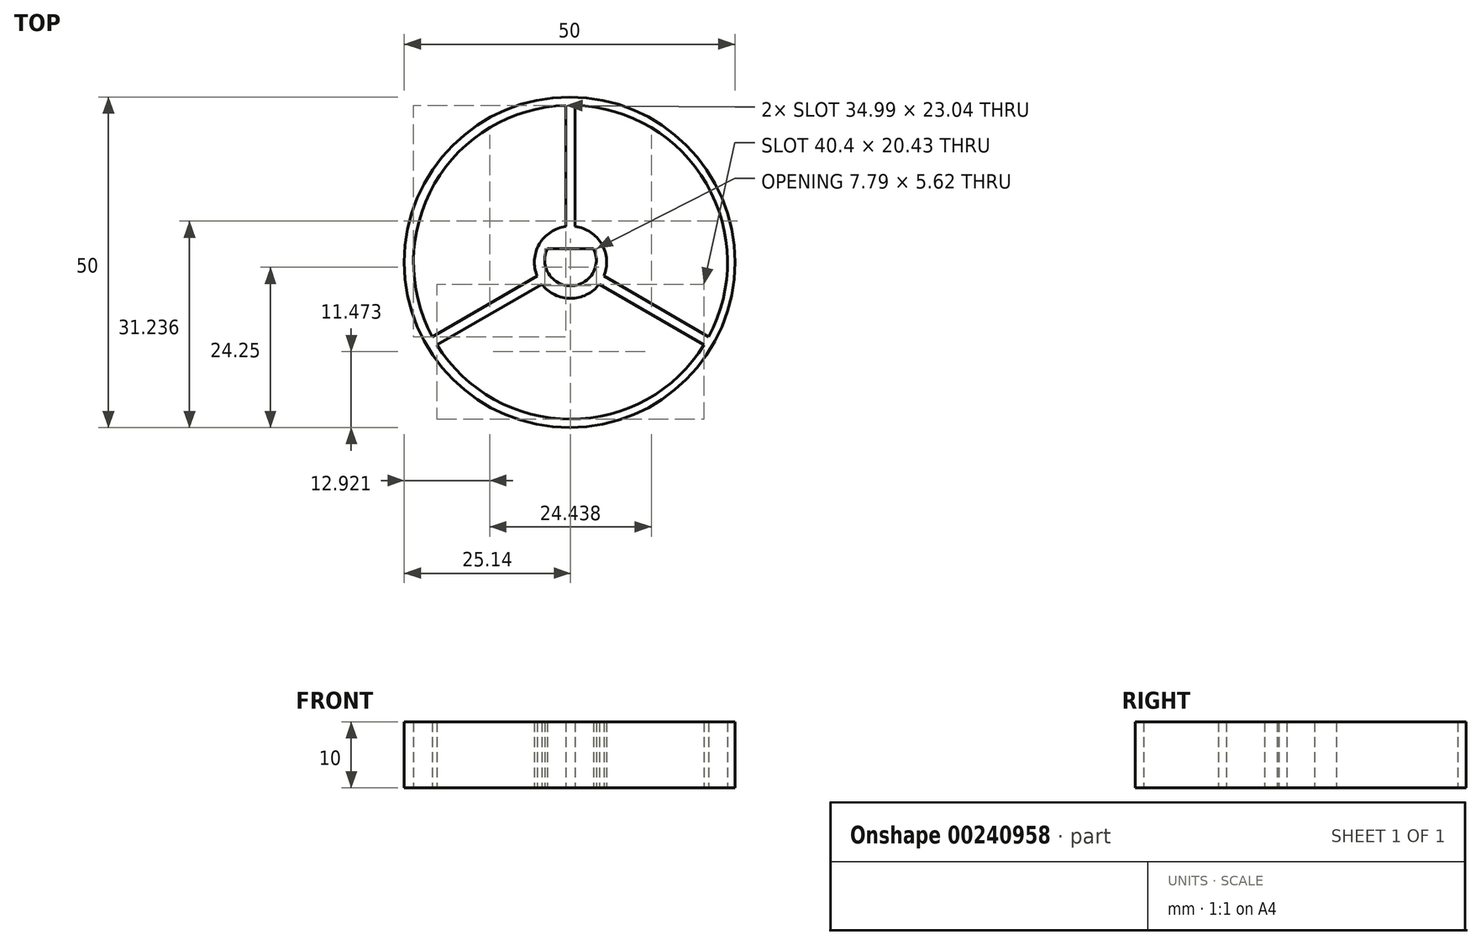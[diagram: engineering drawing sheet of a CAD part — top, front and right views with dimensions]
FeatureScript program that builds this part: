
annotation { "Feature Type Name" : "Feature", "Feature Type Description" : "" }
export const myFeature = defineFeature(function(context is Context, id is Id, definition is map)
    precondition{}
    {
        {
            var Q0;
            Q0=qCreatedBy(makeId("Top.planeOp"),FACE);
            var sketch = newSketch(context, id + "F0", { "sketchPlane" : qUnion([Q0])});
            skCircle(sketch, "E0", {"center": v(0, 0) * mm, "radius": 23.74 * mm});
            skCircle(sketch, "E1", {"center": v(0, 0) * mm, "radius": 5.46 * mm});
            skCircle(sketch, "E2", {"center": v(-0.14, 0) * mm, "radius": 25 * mm});
            skLineSegment(sketch, "E3", {"start": v(0, 0) * mm, "end": v(0, 2.06) * mm});
            skLineSegment(sketch, "E4", {"start": v(0, 2.06) * mm, "end": v(3.5, 2.06) * mm});
            skLineSegment(sketch, "E5.MirrorCS", {"start": v(0, 2.06) * mm, "end": v(-3.5, 2.06) * mm});
            skLineSegment(sketch, "E6", {"start": v(0, 0) * mm, "end": v(-0.69, 0) * mm});
            skArc(sketch, "E7", {"start": v(-3.5, 2.06) * mm, "mid": v(0, -3.56) * mm, "end": v(3.5, 2.06) * mm});
            skLineSegment(sketch, "E8", {"start": v(0, 5.46) * mm, "end": v(0, 8.26) * mm});
            skLineSegment(sketch, "E9", {"start": v(0.7, 5.42) * mm, "end": v(0.7, 23.73) * mm});
            skLineSegment(sketch, "E10.MirrorCS", {"start": v(-0.7, 5.42) * mm, "end": v(-0.7, 23.73) * mm});
            skLineSegment(sketch, "E11.1.0", {"start": v(-4.34, -3.31) * mm, "end": v(-20.2, -12.47) * mm});
            skLineSegment(sketch, "E11.1.1", {"start": v(-4.73, -2.73) * mm, "end": v(-7.15, -4.13) * mm});
            skLineSegment(sketch, "E11.1.2", {"start": v(-5.04, -2.1) * mm, "end": v(-20.9, -11.26) * mm});
            skLineSegment(sketch, "E11.2.0", {"start": v(5.04, -2.1) * mm, "end": v(20.9, -11.26) * mm});
            skLineSegment(sketch, "E11.2.1", {"start": v(4.73, -2.73) * mm, "end": v(7.15, -4.13) * mm});
            skLineSegment(sketch, "E11.2.2", {"start": v(4.34, -3.31) * mm, "end": v(20.2, -12.47) * mm});
            skSolve(sketch);
        }
        {
            var Q0;
            {var subQ3=sQuery(id+"F0.wireOp",EDGE,"9cbbce0d-44af-443e-9ff7-fb77b417e9e4.1.0");Q0=makeQuery(id+"F0.imprint","IMPRINT",FACE,{"disambiguationData":[TD([[makeQuery(id+"F0.imprint","IMPRINT",EDGE,{"derivedFrom":subQ3}),1.0]])]});}
            var Q1;
            {var subQ0=sQuery(id+"F0.wireOp",EDGE,"9cbbce0d-44af-443e-9ff7-fb77b417e9e4.2.0");Q1=makeQuery(id+"F0.imprint","IMPRINT",FACE,{"disambiguationData":[TD([[makeQuery(id+"F0.imprint","IMPRINT",EDGE,{"derivedFrom":subQ0}),1.0]])]});}
            var Q2;
            {var subQ0=sQuery(id+"F0.wireOp",EDGE,"t2yBcWTn-LMue-Bi6q-U126-1WM4RbREa5Lm");Q2=makeQuery(id+"F0.imprint","IMPRINT",FACE,{"disambiguationData":[TD([[makeQuery(id+"F0.imprint","IMPRINT",EDGE,{"derivedFrom":subQ0}),1.0]])]});}
            var Q3;
            Q3=makeQuery(id+"F0.imprint","IMPRINT",FACE,{"disambiguationData":[TD([[makeQuery(id+"F0.imprint","IMPRINT",EDGE,{"derivedFrom":sQuery(id+"F0.wireOp",EDGE,"E2")}),1.0]])]});
            var Q4;
            Q4=makeQuery(id+"F0.imprint","IMPRINT",FACE,{"disambiguationData":[TD([[makeQuery(id+"F0.imprint","IMPRINT",EDGE,{"derivedFrom":sQuery(id+"F0.wireOp",EDGE,"Y1c1QNMm-E33b-wAjd-OVlq-eLRLgHN1sDjT")}),-1.0]])]});
            var Q5;
            Q5=makeQuery(id+"F0.imprint","IMPRINT",FACE,{"disambiguationData":[TD([[makeQuery(id+"F0.imprint","IMPRINT",EDGE,{"derivedFrom":sQuery(id+"F0.wireOp",EDGE,"C1ypOye7-ufjt-MNcX-06jI-t4Vzyp0LE8jm")}),1.0]])]});
            var Q6;
            Q6=makeQuery(id+"F0.imprint","IMPRINT",FACE,{"disambiguationData":[TD([[makeQuery(id+"F0.imprint","IMPRINT",EDGE,{"derivedFrom":sQuery(id+"F0.wireOp",EDGE,"E4")}),1.0]])]});
            var Q7;
            {var subQ0=sQuery(id+"F0.wireOp",EDGE,"E11.1.0");Q7=makeQuery(id+"F0.imprint","IMPRINT",FACE,{"disambiguationData":[TD([[makeQuery(id+"F0.imprint","IMPRINT",EDGE,{"derivedFrom":subQ0}),-1.0]])]});}
            var Q8;
            {var subQ0=sQuery(id+"F0.wireOp",EDGE,"E9");Q8=makeQuery(id+"F0.imprint","IMPRINT",FACE,{"disambiguationData":[TD([[makeQuery(id+"F0.imprint","IMPRINT",EDGE,{"derivedFrom":subQ0}),1.0]])]});}
            var Q9;
            {var subQ0=sQuery(id+"F0.wireOp",EDGE,"E11.2.0");Q9=makeQuery(id+"F0.imprint","IMPRINT",FACE,{"disambiguationData":[TD([[makeQuery(id+"F0.imprint","IMPRINT",EDGE,{"derivedFrom":subQ0}),-1.0]])]});}
            extrude(context, id + "F1", {"entities" : qUnion([Q0, Q1, Q2, Q3, Q4, Q5, Q6, Q7, Q8, Q9]), "depth" : 10 * mm});
        }
    });
